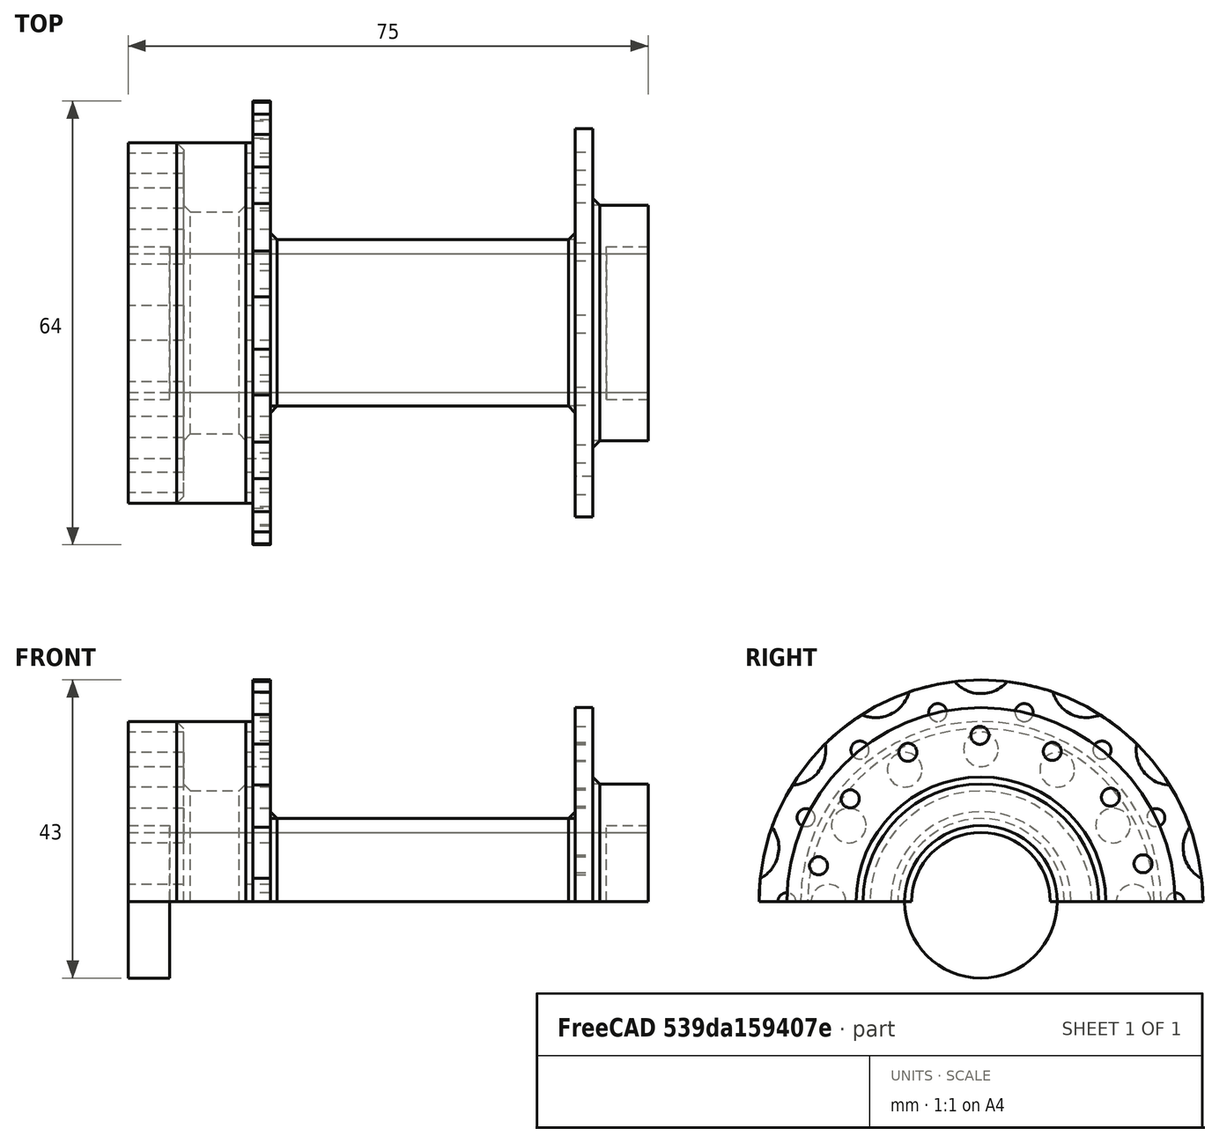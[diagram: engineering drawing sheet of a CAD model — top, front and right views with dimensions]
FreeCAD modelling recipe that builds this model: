
FCSTD DOCUMENT  (FreeCAD 0.16R)
Label: 100mmMTB_wChainline50mmtire_V2
License: All rights reserved
LicenseURL: http://en.wikipedia.org/wiki/All_rights_reserved
objects: Sketcher::SketchObject×8, PartDesign::Pocket×4, PartDesign::PolarPattern×4, PartDesign::Groove×3, PartDesign::Chamfer×2, PartDesign::Revolution×1, Mesh::Feature×1
note: 30 computed .brp shape members not serialized (recipe doc carries the construction recipe); baked Part::Feature solids carry a one-line shape summary decoded from their .brp

FEATURE [Sketcher::SketchObject] Sketch
  sketch-geometry (65):
    g0: LineSegment StartX=31 StartY=10 StartZ=0 EndX=31 EndY=17 EndZ=0
    g1: LineSegment StartX=31 StartY=17 StartZ=0 EndX=23 EndY=17 EndZ=0
    g2: LineSegment StartX=23 StartY=17 StartZ=0 EndX=23 EndY=28 EndZ=0
    g3: LineSegment StartX=23 StartY=28 StartZ=0 EndX=20.5 EndY=28 EndZ=0
    g4: LineSegment StartX=20.5 StartY=28 StartZ=0 EndX=20.5 EndY=12 EndZ=0
    g5: LineSegment StartX=20.5 StartY=12 StartZ=0 EndX=-23.5 EndY=12 EndZ=0
    g6: LineSegment StartX=-23.5 StartY=12 StartZ=0 EndX=-23.5 EndY=32 EndZ=0
    g7: LineSegment StartX=-23.5 StartY=32 StartZ=0 EndX=-26 EndY=32 EndZ=0
    g8: LineSegment StartX=-26 StartY=32 StartZ=0 EndX=-26 EndY=26 EndZ=0
    g9: LineSegment StartX=-44 StartY=26 StartZ=0 EndX=-44 EndY=10 EndZ=0
    g10: LineSegment StartX=-44 StartY=26 StartZ=0 EndX=-26 EndY=26 EndZ=0
    g11: LineSegment [constr] StartX=-45.6 StartY=60 StartZ=0 EndX=-44 EndY=60 EndZ=0
    g12: LineSegment [constr] StartX=-44 StartY=60 StartZ=0 EndX=-44 EndY=20 EndZ=0
    g13: LineSegment [constr] StartX=-44 StartY=20 StartZ=0 EndX=-45.6 EndY=20 EndZ=0
    g14: LineSegment [constr] StartX=-45.6 StartY=20 StartZ=0 EndX=-45.6 EndY=60 EndZ=0
    g15: LineSegment [constr] StartX=0 StartY=0 StartZ=0 EndX=0 EndY=193 EndZ=0
    g16: LineSegment [constr] StartX=-26 StartY=32 StartZ=0 EndX=0 EndY=193 EndZ=0
    g17: LineSegment [constr] StartX=23 StartY=28 StartZ=0 EndX=0 EndY=193 EndZ=0
    g18: LineSegment StartX=-44 StartY=10 StartZ=0 EndX=31 EndY=10 EndZ=0
    g19: Circle [constr] CenterX=0 CenterY=229 CenterZ=0 NormalX=0 NormalY=0 NormalZ=1 Radius=25
    g20: LineSegment [constr] StartX=-30 StartY=331 StartZ=0 EndX=30 EndY=331 EndZ=0
    g21: LineSegment [constr] StartX=30 StartY=299 StartZ=0 EndX=-30 EndY=299 EndZ=0
    g22: LineSegment [constr] StartX=-30 StartY=299 StartZ=0 EndX=-30 EndY=331 EndZ=0
    g23: LineSegment [constr] StartX=36 StartY=379 StartZ=0 EndX=33 EndY=379 EndZ=0
    g24: LineSegment [constr] StartX=33 StartY=379 StartZ=0 EndX=33 EndY=251 EndZ=0
    g25: LineSegment [constr] StartX=33 StartY=251 StartZ=0 EndX=36 EndY=251 EndZ=0
    g26: LineSegment [constr] StartX=30 StartY=331 StartZ=0 EndX=30 EndY=315 EndZ=0
    g27: LineSegment [constr] StartX=30 StartY=315 StartZ=0 EndX=30 EndY=299 EndZ=0
    g28: LineSegment [constr] StartX=36 StartY=379 StartZ=0 EndX=36 EndY=315 EndZ=0
    g29: LineSegment [constr] StartX=36 StartY=315 StartZ=0 EndX=36 EndY=251 EndZ=0
    g30: LineSegment [constr] StartX=30 StartY=315 StartZ=0 EndX=110 EndY=315 EndZ=0
    g31: LineSegment [constr] StartX=-44 StartY=60 StartZ=0 EndX=-44 EndY=42 EndZ=0
    g32: LineSegment [constr] StartX=-25 StartY=254 StartZ=0 EndX=25 EndY=254 EndZ=0
    g33: LineSegment [constr] StartX=29.1959 StartY=240.735 StartZ=0 EndX=27.738 EndY=207.933 EndZ=0
    g34: LineSegment [constr] StartX=34.5926 StartY=204.506 StartZ=0 EndX=33.1835 EndY=172.8 EndZ=0
    g35: LineSegment [constr] StartX=36 StartY=315 StartZ=0 EndX=36 EndY=-60.2245 EndZ=0
    g36: Circle [constr] CenterX=0 CenterY=229 CenterZ=0 NormalX=0 NormalY=0 NormalZ=1 Radius=31.75
    g37: Circle [constr] CenterX=0 CenterY=229 CenterZ=0 NormalX=0 NormalY=0 NormalZ=1 Radius=29.3
    g38: LineSegment [constr] StartX=-50 StartY=69.4665 StartZ=0 EndX=-53.2 EndY=69.4665 EndZ=0
    g39: LineSegment [constr] StartX=-53.2 StartY=69.4665 StartZ=0 EndX=-53.2 EndY=0.090679 EndZ=0
    g40: LineSegment [constr] StartX=-53.2 StartY=0.090679 StartZ=0 EndX=-50 EndY=0.090679 EndZ=0
    g41: LineSegment [constr] StartX=-50 StartY=0.090679 StartZ=0 EndX=-50 EndY=69.4665 EndZ=0
    g42: LineSegment [constr] StartX=-28.5943 StartY=215.201 StartZ=0 EndX=-50.0989 EndY=76.3177 EndZ=0
    g43: LineSegment [constr] StartX=20.3595 StartY=203.492 StartZ=0 EndX=46.7509 EndY=48.3487 EndZ=0
    g44: LineSegment [constr] StartX=29.1431 StartY=211.487 StartZ=0 EndX=56.1775 EndY=52.564 EndZ=0
    g45: LineSegment [constr] StartX=50 StartY=54.306 StartZ=0 EndX=53.2 EndY=54.306 EndZ=0
    g46: LineSegment [constr] StartX=53.2 StartY=54.306 StartZ=0 EndX=53.2 EndY=-0.259602 EndZ=0
    g47: LineSegment [constr] StartX=53.2 StartY=-0.259602 StartZ=0 EndX=50 EndY=-0.259602 EndZ=0
    g48: LineSegment [constr] StartX=50 StartY=-0.259602 StartZ=0 EndX=50 EndY=54.306 EndZ=0
    g49: LineSegment [constr] StartX=42 StartY=315 StartZ=0 EndX=42 EndY=185 EndZ=0
    g50: LineSegment [constr] StartX=-44 StartY=315 StartZ=0 EndX=-44 EndY=185 EndZ=0
    g51: Circle [constr] CenterX=0 CenterY=206.598 CenterZ=0 NormalX=0 NormalY=0 NormalZ=1 Radius=13.75
    g52: Circle [constr] CenterX=-56.5 CenterY=60.4963 CenterZ=0 NormalX=0 NormalY=0 NormalZ=1 Radius=2.75
    g53: Circle [constr] CenterX=-56 CenterY=26.5 CenterZ=0 NormalX=0 NormalY=0 NormalZ=1 Radius=2.75
    g54: Circle [constr] CenterX=-54.5 CenterY=60.4963 CenterZ=0 NormalX=0 NormalY=0 NormalZ=1 Radius=2.75
    g55: Circle [constr] CenterX=-54 CenterY=26.5 CenterZ=0 NormalX=0 NormalY=0 NormalZ=1 Radius=2.75
    g56: LineSegment [constr] StartX=-25.6019 StartY=40.7379 StartZ=0 EndX=-26.8187 EndY=33.2029 EndZ=0
    g57: LineSegment [constr] StartX=-26 StartY=35 StartZ=0 EndX=-23.5 EndY=35 EndZ=0
    g58: LineSegment [constr] StartX=-23.5 StartY=35 StartZ=0 EndX=-23.5 EndY=32.9 EndZ=0
    g59: LineSegment [constr] StartX=-23.5 StartY=32.9 StartZ=0 EndX=-26 EndY=32.9 EndZ=0
    g60: LineSegment [constr] StartX=-26 StartY=32.9 StartZ=0 EndX=-26 EndY=35 EndZ=0
    g61: LineSegment [constr] StartX=20.5 StartY=22.4 StartZ=0 EndX=23 EndY=22.4 EndZ=0
    g62: LineSegment [constr] StartX=23 StartY=22.4 StartZ=0 EndX=23 EndY=24.5 EndZ=0
    g63: LineSegment [constr] StartX=23 StartY=24.5 StartZ=0 EndX=20.5 EndY=24.5 EndZ=0
    g64: LineSegment [constr] StartX=20.5 StartY=24.5 StartZ=0 EndX=20.5 EndY=22.4 EndZ=0
  constraints (170):
    c: Vertical(g2)
    c: Coincident(g2,g3)
    c: Horizontal(g3)
    c: Coincident(g3,g4)
    c: Vertical(g4)
    c: Horizontal(g5)
    c: Vertical(g6)
    c: Coincident(g6,g7)
    c: Horizontal(g1)
    c: Horizontal(g7)
    c: Vertical(g0)
    c: DistanceY(g-1,g1) = 17
    c: DistanceX(g3,g3) = 2.5
    c: DistanceX(g1,g1) = 8
    c: DistanceY(g-1,g5) = 12
    c: DistanceX(g7,g7) = 2.5
    c: DistanceY(g-1,g3) = 28
    c: Coincident(g7,g8)
    c: Vertical(g9)
    c: Vertical(g8)
    c: DistanceY(g7) = 32
    c: DistanceY(g9) = 26
    c: DistanceX(g9,g8) = 18
    c: Horizontal(g10)
    c: Coincident(g10,g9)
    c: Coincident(g10,g8)
    c: Coincident(g11,g12)
    c: Coincident(g12,g13)
    c: Coincident(g13,g14)
    c: Coincident(g14,g11)
    c: Horizontal(g11)
    c: Horizontal(g13)
    c: Vertical(g12)
    c: Vertical(g14)
    c: DistanceX(g11,g11) = 1.6
    c: PointOnObject(g15,g-1)
    c: Vertical(g15)
    c: Distance(g15) = 193
    c: Coincident(g16,g15)
    c: Coincident(g16,g17)
    c: Coincident(g17,g2)
    c: Coincident(g16,g7)
    c: Coincident(g1,g0)
    c: Horizontal(g18)
    c: DistanceY(g18) = 10
    c: DistanceX(g18,g18) = 75
    c: DistanceX(g18,g15) = 44
    c: DistanceY(g12) = 20
    c: PointOnObject(g12,g9)
    c: Coincident(g-1,g15)
    c: Radius(g19) = 25
    c: PointOnObject(g19,g-2)
    c: Coincident(g21,g22)
    c: Coincident(g22,g20)
    c: Horizontal(g20)
    c: Horizontal(g21)
    c: Vertical(g22)
    c: Symmetric(g21,g21,g-2)
    c: Distance(g20) = 60
    c: Coincident(g23,g24)
    c: Coincident(g24,g25)
    c: Horizontal(g23)
    c: Horizontal(g25)
    c: Vertical(g24)
    c: Distance(g25) = 3
    c: Distance(g24) = 128
    c: Vertical(g26)
    c: Coincident(g27,g26)
    c: Coincident(g26,g20)
    c: Coincident(g27,g21)
    c: Symmetric(g20,g21,g26)
    c: Vertical(g28)
    c: Coincident(g29,g25)
    c: Coincident(g28,g23)
    c: Vertical(g29)
    c: Coincident(g29,g28)
    c: Horizontal(g30)
    c: Coincident(g30,g26)
    c: Distance(g30) = 80
    c: PointOnObject(g28,g30)
    c: DistanceX(g26,g28) = 6
    c: Vertical(g31)
    c: PointOnObject(g31,g12)
    c: Coincident(g31,g11)
    c: DistanceY(g11) = 60
    c: DistanceY(g26) = 315
    c: Distance(g22) = 32
    c: Symmetric(g25,g23,g30)
    c: Tangent(g32,g19)
    c: Horizontal(g32)
    c: Symmetric(g32,g32,g-2)
    c: DistanceY(g-1,g32) = 254
    c: Distance(g32) = 50
    c: Coincident(g35,g28)
    c: Vertical(g35)
    c: Radius(g36) = 31.75
    c: Coincident(g36,g19)
    c: Coincident(g37,g19)
    c: Radius(g37) = 29.3
    c: Coincident(g38,g39)
    c: Coincident(g39,g40)
    c: Coincident(g40,g41)
    c: Coincident(g41,g38)
    c: Horizontal(g38)
    c: Horizontal(g40)
    c: Vertical(g39)
    c: Vertical(g41)
    c: Distance(g40) = 3.2
    c: PointOnObject(g42,g36)
    c: Distance(g44,g43) = 10
    c: Parallel(g44,g43)
    c: Coincident(g45,g46)
    c: Coincident(g46,g47)
    c: Coincident(g47,g48)
    c: Coincident(g48,g45)
    c: Horizontal(g45)
    c: Horizontal(g47)
    c: Vertical(g46)
    c: Vertical(g48)
    c: Distance(g45) = 3.2
    c: Vertical(g49)
    c: Distance(g49) = 130
    c: PointOnObject(g49,g30)
    c: Distance(g49,g28) = 6
    c: Vertical(g50)
    c: Distance(g50) = 130
    c: PointOnObject(g50,g30)
    c: Distance(g50,g22) = 14
    c: Radius(g51) = 13.75
    c: PointOnObject(g51,g15)
    c: Radius(g52) = 2.75
    c: Equal(g52,g53)
    c: DistanceY(g-1,g53) = 26.5
    c: Radius(g55) = 2.75
    c: Equal(g55,g54)
    c: DistanceY(g55) = 26.5
    c: Parallel(g56,g16)
    c: Distance(g56,g16) = 1
    c: Coincident(g5,g6)
    c: Coincident(g4,g5)
    c: Distance(g55,g53) = 2
    c: Coincident(g57,g58)
    c: Coincident(g58,g59)
    c: Coincident(g59,g60)
    c: Coincident(g60,g57)
    c: Horizontal(g57)
    c: Horizontal(g59)
    c: Vertical(g58)
    c: Vertical(g60)
    c: Distance(g58) = 2.1
    c: PointOnObject(g57,g8)
    c: PointOnObject(g57,g6)
    c: Distance(g57,g6) = 3
    c: Coincident(g61,g62)
    c: Coincident(g62,g63)
    c: Coincident(g63,g64)
    c: Coincident(g64,g61)
    c: Horizontal(g61)
    c: Horizontal(g63)
    c: Vertical(g62)
    c: Vertical(g64)
    c: PointOnObject(g62,g2)
    c: Distance(g64) = 2.1
    c: PointOnObject(g63,g4)
    c: Distance(g62,g2) = 3.5
    c: Distance(g55,g41) = 4
    c: Coincident(g2,g1)
    c: PointOnObject(g0,g18)
    c: Coincident(g18,g0)
    c: Coincident(g18,g9)
FEATURE [PartDesign::Revolution] Revolution
  Angle = 180
  Axis = (1,0,0)
  Base = (0,0,0)
  ReferenceAxis = -> Sketch [H_Axis]
  Sketch = -> Sketch
FEATURE [Sketcher::SketchObject] Sketch001
  ExternalGeometry = -> [Revolution]
  Placement = pos=(0,0,0) rot=(1,0,0;3.14159rad)
  Support = -> Revolution [Face13]
  sketch-geometry (4):
    g0: LineSegment StartX=-44 StartY=11 StartZ=0 EndX=-38 EndY=11 EndZ=0
    g1: LineSegment StartX=-38 StartY=11 StartZ=0 EndX=-38 EndY=0 EndZ=0
    g2: LineSegment StartX=-38 StartY=0 StartZ=0 EndX=-44 EndY=0 EndZ=0
    g3: LineSegment StartX=-44 StartY=0 StartZ=0 EndX=-44 EndY=11 EndZ=0
  constraints (12):
    c: Coincident(g0,g1)
    c: Coincident(g1,g2)
    c: Coincident(g2,g3)
    c: Coincident(g3,g0)
    c: Horizontal(g0)
    c: Horizontal(g2)
    c: Vertical(g1)
    c: Vertical(g3)
    c: Distance(g0) = 6
    c: PointOnObject(g1,g-1)
    c: PointOnObject(g0,g-3)
    c: DistanceY(g0) = 11
FEATURE [PartDesign::Groove] Groove
  Angle = 360
  Axis = (1,0,0)
  Base = (0,0,0)
  ReferenceAxis = -> Sketch001 [H_Axis]
  Reversed = true
  Sketch = -> Sketch001
FEATURE [Sketcher::SketchObject] Sketch002
  ExternalGeometry = -> [Groove]
  Placement = pos=(0,0,0) rot=(1,0,0;3.14159rad)
  Support = -> Groove [Face5]
  sketch-geometry (4):
    g0: LineSegment StartX=-36 StartY=16 StartZ=0 EndX=-27 EndY=16 EndZ=0
    g1: LineSegment StartX=-27 StartY=16 StartZ=0 EndX=-27 EndY=26 EndZ=0
    g2: LineSegment StartX=-27 StartY=26 StartZ=0 EndX=-36 EndY=26 EndZ=0
    g3: LineSegment StartX=-36 StartY=26 StartZ=0 EndX=-36 EndY=16 EndZ=0
  constraints (12):
    c: Coincident(g0,g1)
    c: Coincident(g1,g2)
    c: Coincident(g2,g3)
    c: Coincident(g3,g0)
    c: Horizontal(g0)
    c: Horizontal(g2)
    c: Vertical(g1)
    c: Vertical(g3)
    c: PointOnObject(g2,g-4)
    c: Distance(g2,g-4) = 8
    c: Distance(g1,g-4) = 1
    c: Distance(g1) = 10
FEATURE [PartDesign::Groove] Groove001
  Angle = 360
  Axis = (1,0,0)
  Base = (0,0,0)
  ReferenceAxis = -> Sketch002 [H_Axis]
  Reversed = true
  Sketch = -> Sketch002
FEATURE [PartDesign::Chamfer] Chamfer
  Base = -> Groove001 [Edge45,Edge52,Edge53,Edge47,Edge46]
  Size = 1
FEATURE [Sketcher::SketchObject] Sketch003
  Placement = pos=(-44,0,0) rot=(0.57735,-0.57735,-0.57735;2.0944rad)
  Support = -> Chamfer [Face4]
  sketch-geometry (1):
    g0: Circle CenterX=-22 CenterY=0 CenterZ=0 NormalX=0 NormalY=0 NormalZ=1 Radius=2.5
  constraints (3):
    c: Radius(g0) = 2.5
    c: Distance(g-1,g0) = 22
    c: PointOnObject(g0,g-1)
FEATURE [PartDesign::Pocket] Pocket
  Length = 24
  Sketch = -> Sketch003
  Type = 0
FEATURE [PartDesign::PolarPattern] PolarPattern
  Angle = 360
  Axis = -> Sketch003 [N_Axis]
  Occurrences = 12
  Originals = -> [Pocket]
FEATURE [Sketcher::SketchObject] Sketch004
  Placement = pos=(-26,0,0) rot=(0.57735,-0.57735,-0.57735;2.0944rad)
  Support = -> PolarPattern [Face43]
  sketch-geometry (1):
    g0: Circle CenterX=-28 CenterY=0 CenterZ=0 NormalX=0 NormalY=0 NormalZ=1 Radius=1.3
  constraints (3):
    c: PointOnObject(g0,g-1)
    c: Radius(g0) = 1.3
    c: Distance(g-1,g0) = 28
FEATURE [PartDesign::Pocket] Pocket001
  Length = 5
  Sketch = -> Sketch004
  Type = 0
FEATURE [PartDesign::PolarPattern] PolarPattern001
  Angle = 360
  Axis = -> Sketch004 [N_Axis]
  Occurrences = 14
  Originals = -> [Pocket001]
FEATURE [Sketcher::SketchObject] Sketch005
  Placement = pos=(23,0,0) rot=(0.57735,0.57735,0.57735;2.0944rad)
  Support = -> PolarPattern001 [Face28]
  sketch-geometry (1):
    g0: Circle CenterX=-23.4309 CenterY=5.19535 CenterZ=0 NormalX=0 NormalY=0 NormalZ=1 Radius=1.3
  constraints (2):
    c: Radius(g0) = 1.3
    c: Distance(g-1,g0) = 24
FEATURE [PartDesign::Pocket] Pocket002
  Length = 5
  Sketch = -> Sketch005
  Type = 0
FEATURE [PartDesign::PolarPattern] PolarPattern002
  Angle = 360
  Axis = -> Sketch005 [N_Axis]
  Occurrences = 14
  Originals = -> [Pocket002]
FEATURE [Sketcher::SketchObject] Sketch006
  ExternalGeometry = -> [PolarPattern002]
  Placement = pos=(0,0,0) rot=(1,0,0;3.14159rad)
  Support = -> PolarPattern002 [Face8]
  sketch-geometry (4):
    g0: LineSegment StartX=25 StartY=11 StartZ=0 EndX=31 EndY=11 EndZ=0
    g1: LineSegment StartX=31 StartY=11 StartZ=0 EndX=31 EndY=0.998738 EndZ=0
    g2: LineSegment StartX=31 StartY=0.998738 StartZ=0 EndX=25 EndY=0.998738 EndZ=0
    g3: LineSegment StartX=25 StartY=0.998738 StartZ=0 EndX=25 EndY=11 EndZ=0
  constraints (11):
    c: Coincident(g0,g1)
    c: Coincident(g1,g2)
    c: Coincident(g2,g3)
    c: Coincident(g3,g0)
    c: Horizontal(g0)
    c: Horizontal(g2)
    c: Vertical(g1)
    c: Vertical(g3)
    c: Distance(g0) = 6
    c: DistanceY(g0) = 11
    c: PointOnObject(g0,g-4)
FEATURE [PartDesign::Groove] Groove002
  Angle = 360
  Axis = (1,0,0)
  Base = (0,0,0)
  ReferenceAxis = -> Sketch006 [H_Axis]
  Reversed = true
  Sketch = -> Sketch006
FEATURE [PartDesign::Chamfer] Chamfer001
  Base = -> Groove002 [Edge127]
  Size = 1
FEATURE [Sketcher::SketchObject] Sketch007
  Placement = pos=(-26,0,0) rot=(0.57735,-0.57735,-0.57735;2.0944rad)
  Support = -> Chamfer001 [Face63]
  sketch-geometry (1):
    g0: Circle CenterX=-34.152 CenterY=7.79204 CenterZ=0 NormalX=0 NormalY=0 NormalZ=1 Radius=5
  constraints (1):
    c: Radius(g0) = 5
FEATURE [PartDesign::Pocket] Pocket003
  Length = 5
  Sketch = -> Sketch007
  Type = 1
FEATURE [PartDesign::PolarPattern] PolarPattern003
  Angle = 360
  Axis = -> Sketch007 [N_Axis]
  Occurrences = 14
  Originals = -> [Pocket003]
FEATURE [Mesh::Feature] Mesh  label="PolarPattern003 (Meshed)"
